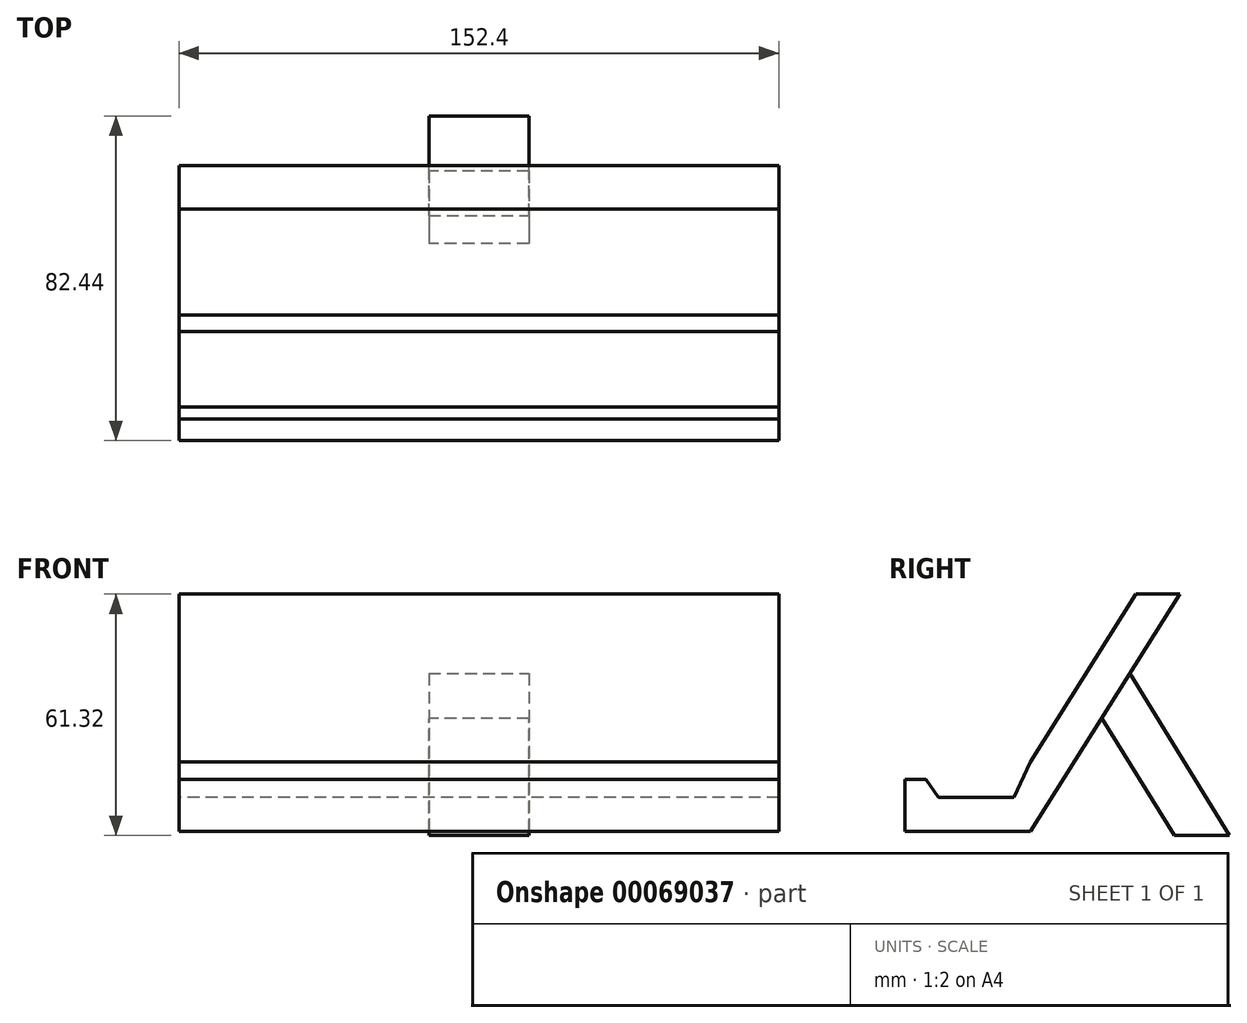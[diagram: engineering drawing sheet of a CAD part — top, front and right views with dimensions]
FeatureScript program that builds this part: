
annotation { "Feature Type Name" : "Feature", "Feature Type Description" : "" }
export const myFeature = defineFeature(function(context is Context, id is Id, definition is map)
    precondition{}
    {
        {
            var Q0;
            Q0=qCreatedBy(makeId("Right.planeOp"),FACE);
            var sketch = newSketch(context, id + "F0", { "sketchPlane" : qUnion([Q0])});
            skLineSegment(sketch, "E0", {"start": v(0, 0) * mm, "end": v(26.81, 42.64) * mm});
            skLineSegment(sketch, "E1", {"start": v(26.81, 42.64) * mm, "end": v(37.94, 42.64) * mm});
            skLineSegment(sketch, "E2", {"start": v(37.94, 42.64) * mm, "end": v(0, -17.7) * mm});
            skLineSegment(sketch, "E3", {"start": v(0, -17.7) * mm, "end": v(-31.95, -17.7) * mm});
            skLineSegment(sketch, "E4", {"start": v(-31.95, -17.7) * mm, "end": v(-31.95, -4.42) * mm});
            skLineSegment(sketch, "E5", {"start": v(-31.95, -4.42) * mm, "end": v(-26.53, -4.42) * mm});
            skLineSegment(sketch, "E6", {"start": v(-26.53, -4.42) * mm, "end": v(-23.39, -8.99) * mm});
            skLineSegment(sketch, "E7", {"start": v(-23.39, -8.99) * mm, "end": v(-4.28, -8.99) * mm});
            skLineSegment(sketch, "E8", {"start": v(-4.28, -8.99) * mm, "end": v(0, 0) * mm});
            skSolve(sketch);
        }
        {
            var Q0;
            Q0 = qSketchRegion(id + "F0", true);
            extrude(context, id + "F1", {"entities" : qUnion([Q0]), "depth" : 76.2 * mm, "hasSecondDirection" : true, "secondDirectionOppositeDirection" : true, "secondDirectionDepth" : 76.2 * mm});
        }
        {
            var Q0;
            Q0=qCreatedBy(makeId("Right.planeOp"),FACE);
            var sketch = newSketch(context, id + "F2", { "sketchPlane" : qUnion([Q0])});
            skLineSegment(sketch, "E9", {"start": v(24.53, 23.53) * mm, "end": v(50.49, -18.68) * mm});
            skLineSegment(sketch, "E10", {"start": v(50.49, -18.68) * mm, "end": v(36.51, -18.68) * mm});
            skLineSegment(sketch, "E11", {"start": v(36.51, -18.68) * mm, "end": v(16.54, 13.55) * mm});
            skLineSegment(sketch, "E12", {"start": v(16.54, 13.55) * mm, "end": v(24.53, 23.53) * mm});
            skSolve(sketch);
        }
        {
            var Q0;
            Q0 = qSketchRegion(id + "F2", true);
            extrude(context, id + "F3", {"entities" : qUnion([Q0]), "operationType" : NewBodyOperationType.ADD, "depth" : 12.7 * mm, "hasSecondDirection" : true, "secondDirectionOppositeDirection" : true, "secondDirectionDepth" : 12.7 * mm});
        }
    });
